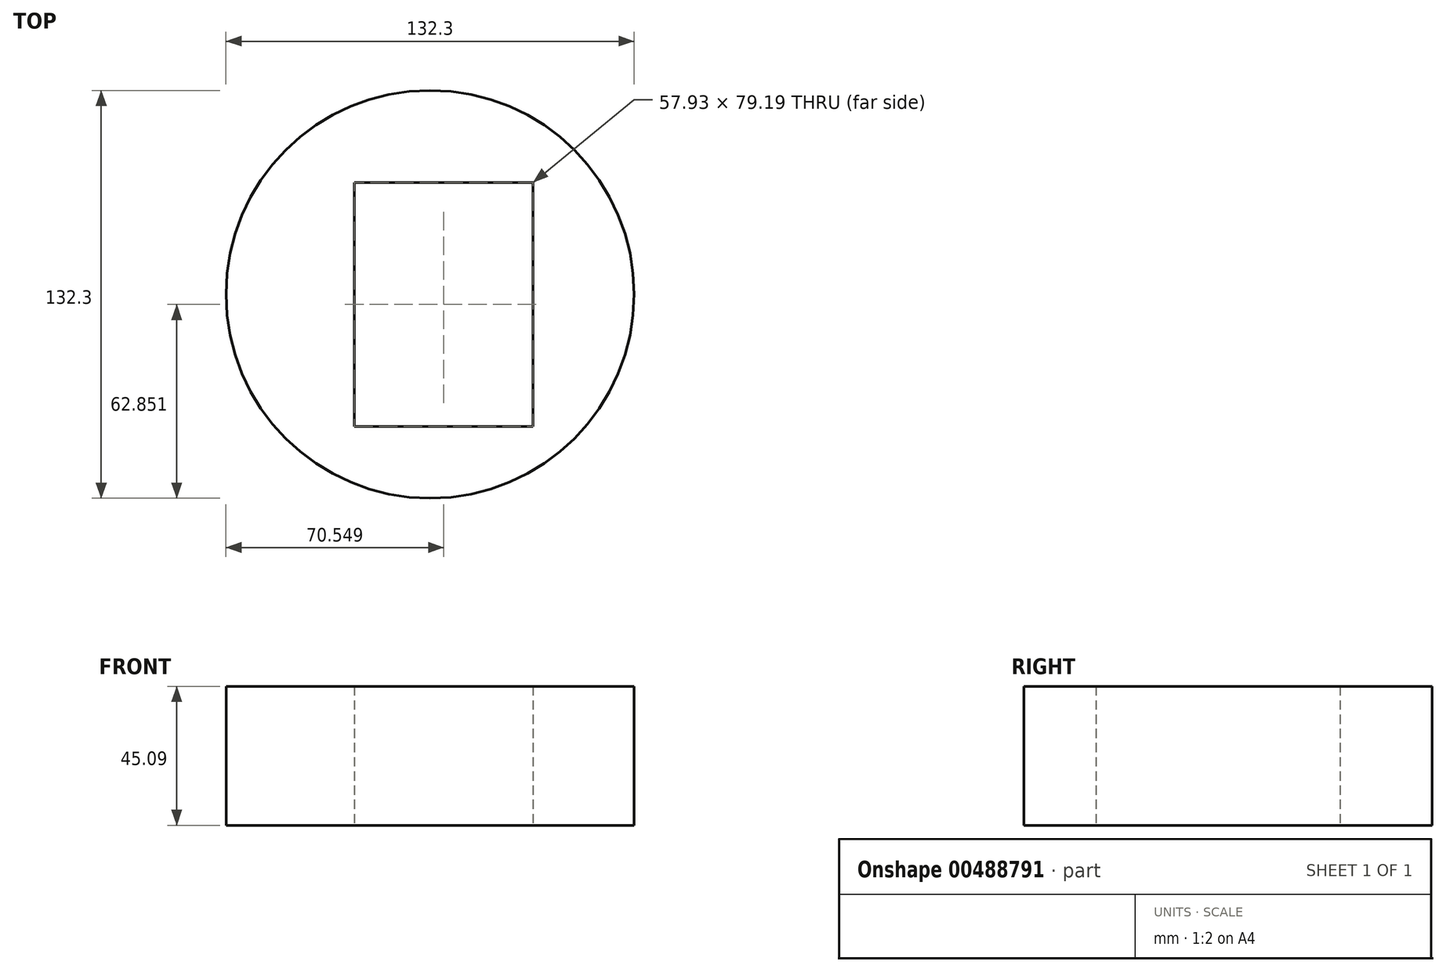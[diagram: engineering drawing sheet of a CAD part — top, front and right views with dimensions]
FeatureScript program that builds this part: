
annotation { "Feature Type Name" : "Feature", "Feature Type Description" : "" }
export const myFeature = defineFeature(function(context is Context, id is Id, definition is map)
    precondition{}
    {
        {
            var Q0;
            Q0=qCreatedBy(makeId("Top.planeOp"),FACE);
            var sketch = newSketch(context, id + "F0", { "sketchPlane" : qUnion([Q0])});
            skCircle(sketch, "E0", {"center": v(0, 0) * mm, "radius": 66.15 * mm});
            skLineSegment(sketch, "E1.bottom", {"start": v(33.36, 36.3) * mm, "end": v(-24.56, 36.3) * mm});
            skLineSegment(sketch, "E1.top", {"start": v(33.36, -42.9) * mm, "end": v(-24.56, -42.9) * mm});
            skLineSegment(sketch, "E1.left", {"start": v(33.36, 36.3) * mm, "end": v(33.36, -42.9) * mm});
            skLineSegment(sketch, "E1.right", {"start": v(-24.56, 36.3) * mm, "end": v(-24.56, -42.9) * mm});
            skPoint(sketch, "E1.middle", {"position": v(4.4, -3.3) * mm});
            skSolve(sketch);
        }
        {
            var Q0;
            Q0 = qSketchRegion(id + "F0", true);
            extrude(context, id + "F1", {"entities" : qUnion([Q0]), "depth" : 45.1 * mm});
        }
    });
